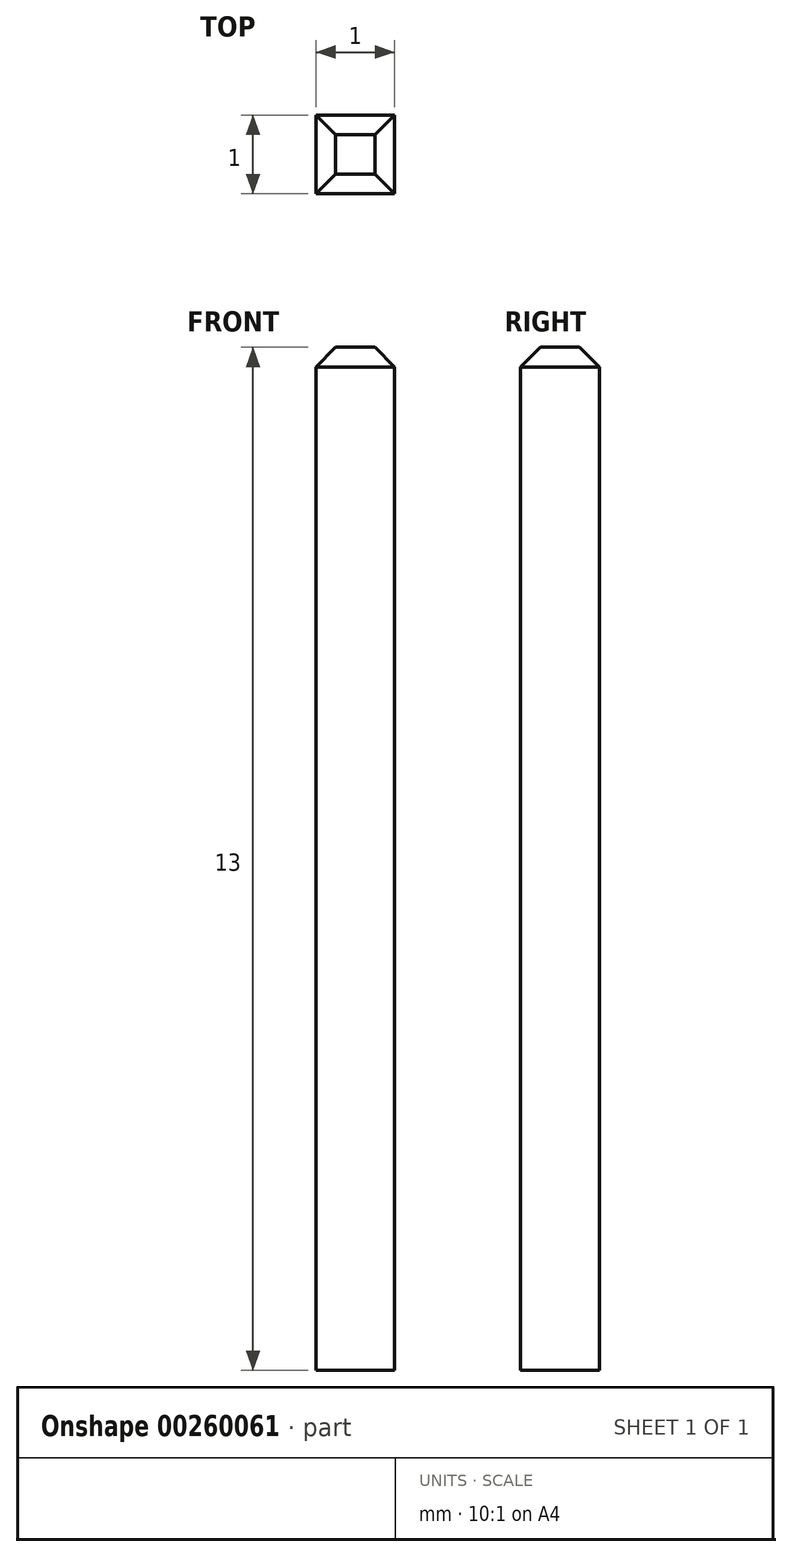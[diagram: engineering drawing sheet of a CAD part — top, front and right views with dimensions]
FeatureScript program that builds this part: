
annotation { "Feature Type Name" : "Feature", "Feature Type Description" : "" }
export const myFeature = defineFeature(function(context is Context, id is Id, definition is map)
    precondition{}
    {
        {
            var Q0;
            Q0=qCreatedBy(makeId("Top.planeOp"),FACE);
            var sketch = newSketch(context, id + "F0", { "sketchPlane" : qUnion([Q0])});
            skLineSegment(sketch, "E0.bottom", {"start": v(0, 0) * mm, "end": v(1, 0) * mm});
            skLineSegment(sketch, "E0.top", {"start": v(0, 1) * mm, "end": v(1, 1) * mm});
            skLineSegment(sketch, "E0.left", {"start": v(0, 0) * mm, "end": v(0, 1) * mm});
            skLineSegment(sketch, "E0.right", {"start": v(1, 0) * mm, "end": v(1, 1) * mm});
            skSolve(sketch);
        }
        {
            var Q0;
            Q0=qSketchRegion(id+"F0",true);
            extrude(context, id + "F1", {"entities" : qUnion([Q0]), "depth" : 13 * mm});
        }
        {
            var Q0;
            Q0=makeQuery(id+"F1.opExtrude","CAP_EDGE",EDGE,{"disambiguationData":[OSD([sQuery(id+"F0.wireOp",EDGE,"E0.bottom")])],"isStart":false});
            var Q1;
            Q1=makeQuery(id+"F1.opExtrude","CAP_EDGE",EDGE,{"disambiguationData":[OSD([sQuery(id+"F0.wireOp",EDGE,"E0.right")])],"isStart":false});
            var Q2;
            Q2=makeQuery(id+"F1.opExtrude","CAP_EDGE",EDGE,{"disambiguationData":[OSD([sQuery(id+"F0.wireOp",EDGE,"E0.top")])],"isStart":false});
            var Q3;
            Q3=makeQuery(id+"F1.opExtrude","CAP_EDGE",EDGE,{"disambiguationData":[OSD([sQuery(id+"F0.wireOp",EDGE,"E0.left")])],"isStart":false});
            chamfer(context, id + "F2", {"entities" : qUnion([Q0, Q1, Q2, Q3]), "width" : 0.25 * mm, "tangentPropagation" : true});
        }
    });
